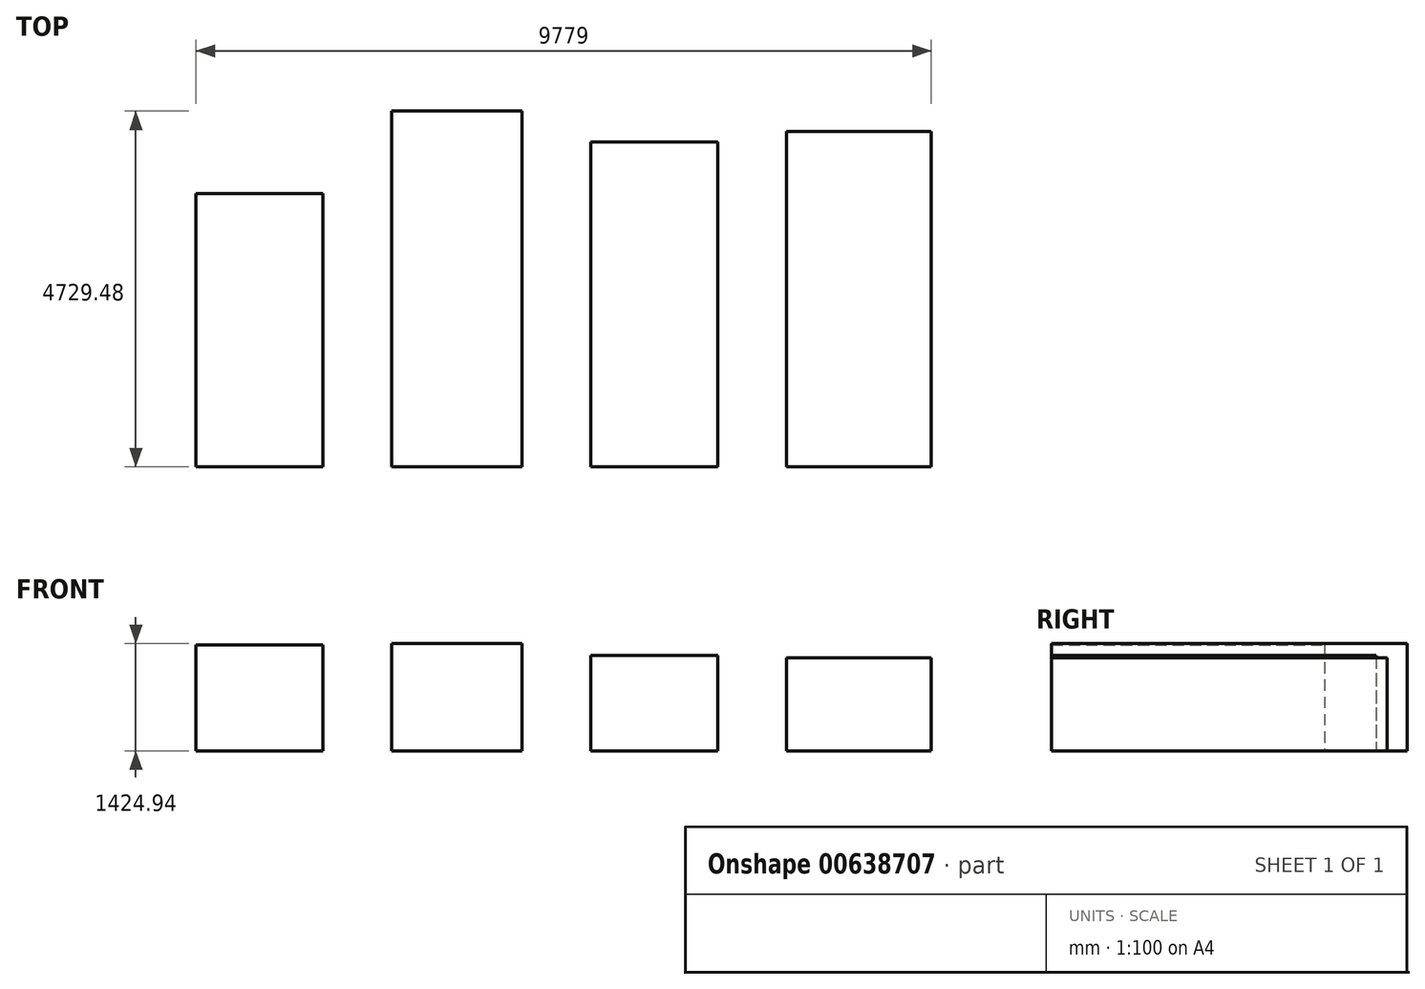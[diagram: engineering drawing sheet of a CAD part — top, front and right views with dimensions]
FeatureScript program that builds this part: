
annotation { "Feature Type Name" : "Feature", "Feature Type Description" : "" }
export const myFeature = defineFeature(function(context is Context, id is Id, definition is map)
    precondition{}
    {
        {
            var Q0;
            Q0=qCreatedBy(makeId("Top.planeOp"),FACE);
            var sketch = newSketch(context, id + "F0", { "sketchPlane" : qUnion([Q0])});
            skLineSegment(sketch, "E0.bottom", {"start": v(0, 0) * mm, "end": v(1689.1, 0) * mm});
            skLineSegment(sketch, "E0.top", {"start": v(0, 3632.2) * mm, "end": v(1689.1, 3632.2) * mm});
            skLineSegment(sketch, "E0.left", {"start": v(0, 0) * mm, "end": v(0, 3632.2) * mm});
            skLineSegment(sketch, "E0.right", {"start": v(1689.1, 0) * mm, "end": v(1689.1, 3632.2) * mm});
            skSolve(sketch);
        }
        {
            var Q0;
            Q0 = qSketchRegion(id + "F0", true);
            extrude(context, id + "F1", {"entities" : qUnion([Q0]), "depth" : 1407.16 * mm, "offsetDistance" : 25.4 * mm});
        }
        {
            var Q0;
            Q0=qCreatedBy(makeId("Top.planeOp"),FACE);
            var sketch = newSketch(context, id + "F2", { "sketchPlane" : qUnion([Q0])});
            skLineSegment(sketch, "E1.bottom", {"start": v(2603.5, 0) * mm, "end": v(4333.24, 0) * mm});
            skLineSegment(sketch, "E1.top", {"start": v(2603.5, 4729.48) * mm, "end": v(4333.24, 4729.48) * mm});
            skLineSegment(sketch, "E1.left", {"start": v(2603.5, 0) * mm, "end": v(2603.5, 4729.48) * mm});
            skLineSegment(sketch, "E1.right", {"start": v(4333.24, 0) * mm, "end": v(4333.24, 4729.48) * mm});
            skSolve(sketch);
        }
        {
            var Q0;
            Q0 = qSketchRegion(id + "F2", true);
            extrude(context, id + "F3", {"entities" : qUnion([Q0]), "depth" : 1424.94 * mm, "offsetDistance" : 25.4 * mm});
        }
        {
            var Q0;
            Q0=qCreatedBy(makeId("Top.planeOp"),FACE);
            var sketch = newSketch(context, id + "F4", { "sketchPlane" : qUnion([Q0])});
            skLineSegment(sketch, "E2.bottom", {"start": v(5247.64, 0) * mm, "end": v(6936.74, 0) * mm});
            skLineSegment(sketch, "E2.top", {"start": v(5247.64, 4315.46) * mm, "end": v(6936.74, 4315.46) * mm});
            skLineSegment(sketch, "E2.left", {"start": v(5247.64, 0) * mm, "end": v(5247.64, 4315.46) * mm});
            skLineSegment(sketch, "E2.right", {"start": v(6936.74, 0) * mm, "end": v(6936.74, 4315.46) * mm});
            skSolve(sketch);
        }
        {
            var Q0;
            Q0 = qSketchRegion(id + "F4", true);
            extrude(context, id + "F5", {"entities" : qUnion([Q0]), "depth" : 1264.92 * mm, "offsetDistance" : 25.4 * mm});
        }
        {
            var Q0;
            Q0=qCreatedBy(makeId("Top.planeOp"),FACE);
            var sketch = newSketch(context, id + "F6", { "sketchPlane" : qUnion([Q0])});
            skLineSegment(sketch, "E3.bottom", {"start": v(7851.14, 0) * mm, "end": v(9779, 0) * mm});
            skLineSegment(sketch, "E3.top", {"start": v(7851.14, 4460.24) * mm, "end": v(9779, 4460.24) * mm});
            skLineSegment(sketch, "E3.left", {"start": v(7851.14, 0) * mm, "end": v(7851.14, 4460.24) * mm});
            skLineSegment(sketch, "E3.right", {"start": v(9779, 0) * mm, "end": v(9779, 4460.24) * mm});
            skSolve(sketch);
        }
        {
            var Q0;
            Q0 = qSketchRegion(id + "F6", true);
            extrude(context, id + "F7", {"entities" : qUnion([Q0]), "depth" : 1236.98 * mm, "offsetDistance" : 25.4 * mm});
        }
    });
